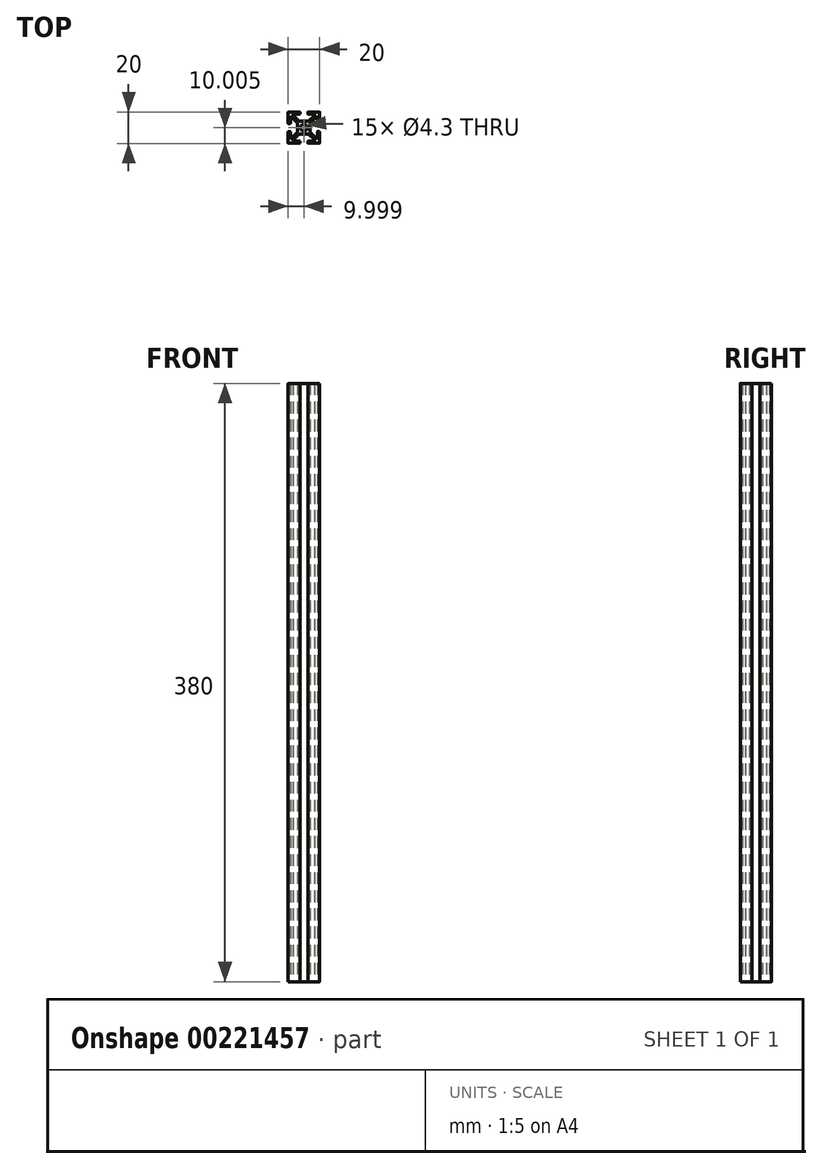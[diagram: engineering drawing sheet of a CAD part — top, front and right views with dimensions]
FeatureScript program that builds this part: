
annotation { "Feature Type Name" : "Feature", "Feature Type Description" : "" }
export const myFeature = defineFeature(function(context is Context, id is Id, definition is map)
    precondition{}
    {
        {
            var Q0;
            Q0=qCreatedBy(makeId("Top.planeOp"),FACE);
            var sketch = newSketch(context, id + "F0", { "sketchPlane" : qUnion([Q0])});
            skLineSegment(sketch, "E0.bottom", {"start": v(-9.92, 8.63) * mm, "end": v(10.08, 8.63) * mm, "construction": true});
            skLineSegment(sketch, "E0.top", {"start": v(-9.92, -11.37) * mm, "end": v(10.08, -11.37) * mm, "construction": true});
            skLineSegment(sketch, "E0.left", {"start": v(-9.92, 8.63) * mm, "end": v(-9.92, -11.37) * mm, "construction": true});
            skLineSegment(sketch, "E0.right", {"start": v(10.08, 8.63) * mm, "end": v(10.08, -11.37) * mm, "construction": true});
            skCircle(sketch, "E1", {"center": v(0.08, -1.37) * mm, "radius": 2.15 * mm});
            skPoint(sketch, "E1.centerSnap0", {"position": v(0.08, 8.63) * mm});
            skPoint(sketch, "E1.centerSnap1", {"position": v(-9.92, -1.37) * mm});
            skLineSegment(sketch, "E2.bottom", {"start": v(-3.92, 2.63) * mm, "end": v(4.08, 2.63) * mm, "construction": true});
            skLineSegment(sketch, "E2.top", {"start": v(-3.92, -5.37) * mm, "end": v(4.08, -5.37) * mm, "construction": true});
            skLineSegment(sketch, "E2.left", {"start": v(-3.92, 2.63) * mm, "end": v(-3.92, -5.37) * mm, "construction": true});
            skLineSegment(sketch, "E2.right", {"start": v(4.08, 2.63) * mm, "end": v(4.08, -5.37) * mm, "construction": true});
            skLineSegment(sketch, "E3", {"start": v(9.88, 8.63) * mm, "end": v(2.78, 8.63) * mm});
            skLineSegment(sketch, "E4.0", {"start": v(6.63, 7.13) * mm, "end": v(2.78, 7.13) * mm});
            skLineSegment(sketch, "E5", {"start": v(4.08, 2.63) * mm, "end": v(10.08, 8.63) * mm, "construction": true});
            skLineSegment(sketch, "E6.0", {"start": v(4.08, 1.57) * mm, "end": v(7.83, 5.33) * mm});
            skLineSegment(sketch, "E7.0", {"start": v(3.02, 2.63) * mm, "end": v(6.77, 6.39) * mm});
            skLineSegment(sketch, "E8", {"start": v(10.08, 8.43) * mm, "end": v(10.08, 1.33) * mm});
            skLineSegment(sketch, "E9.0", {"start": v(8.58, 5.18) * mm, "end": v(8.58, 1.33) * mm});
            skLineSegment(sketch, "E10", {"start": v(8.38, 5.38) * mm, "end": v(7.97, 5.38) * mm});
            skLineSegment(sketch, "E11", {"start": v(6.83, 6.93) * mm, "end": v(6.83, 6.53) * mm});
            skLineSegment(sketch, "E12", {"start": v(2.58, 8.43) * mm, "end": v(2.58, 7.33) * mm});
            skLineSegment(sketch, "E13", {"start": v(8.78, 1.13) * mm, "end": v(9.88, 1.13) * mm});
            skLineSegment(sketch, "E14", {"start": v(0.08, -1.37) * mm, "end": v(10.08, -1.37) * mm, "construction": true});
            skLineSegment(sketch, "E15", {"start": v(0.08, -1.37) * mm, "end": v(0.08, 8.63) * mm, "construction": true});
            skPoint(sketch, "E16.visualSharp", {"position": v(10.08, 8.63) * mm});
            skArc(sketch, "E16.filletArc", {"start": v(10.08, 8.43) * mm, "mid": v(10.02, 8.58) * mm, "end": v(9.88, 8.63) * mm});
            skPoint(sketch, "E17.visualSharp", {"position": v(2.58, 8.63) * mm});
            skArc(sketch, "E17.filletArc", {"start": v(2.78, 8.63) * mm, "mid": v(2.64, 8.58) * mm, "end": v(2.58, 8.43) * mm});
            skPoint(sketch, "E18.visualSharp", {"position": v(2.58, 7.13) * mm});
            skArc(sketch, "E18.filletArc", {"start": v(2.58, 7.33) * mm, "mid": v(2.64, 7.2) * mm, "end": v(2.78, 7.13) * mm});
            skPoint(sketch, "E19.visualSharp", {"position": v(8.58, 1.13) * mm});
            skArc(sketch, "E19.filletArc", {"start": v(8.58, 1.33) * mm, "mid": v(8.64, 1.2) * mm, "end": v(8.78, 1.13) * mm});
            skPoint(sketch, "E20.visualSharp", {"position": v(10.08, 1.13) * mm});
            skArc(sketch, "E20.filletArc", {"start": v(9.88, 1.13) * mm, "mid": v(10.02, 1.2) * mm, "end": v(10.08, 1.33) * mm});
            skPoint(sketch, "E21.visualSharp", {"position": v(6.83, 7.13) * mm});
            skArc(sketch, "E21.filletArc", {"start": v(6.83, 6.93) * mm, "mid": v(6.77, 7.08) * mm, "end": v(6.63, 7.13) * mm});
            skPoint(sketch, "E22.visualSharp", {"position": v(6.83, 6.45) * mm});
            skArc(sketch, "E22.filletArc", {"start": v(6.77, 6.39) * mm, "mid": v(6.81, 6.45) * mm, "end": v(6.83, 6.53) * mm});
            skPoint(sketch, "E23.visualSharp", {"position": v(7.89, 5.38) * mm});
            skArc(sketch, "E23.filletArc", {"start": v(7.97, 5.38) * mm, "mid": v(7.9, 5.37) * mm, "end": v(7.83, 5.33) * mm});
            skPoint(sketch, "E24.visualSharp", {"position": v(8.58, 5.38) * mm});
            skArc(sketch, "E24.filletArc", {"start": v(8.58, 5.18) * mm, "mid": v(8.52, 5.33) * mm, "end": v(8.38, 5.38) * mm});
            skLineSegment(sketch, "E25.MirrorCS", {"start": v(4.08, -4.3) * mm, "end": v(7.83, -8.06) * mm});
            skArc(sketch, "E26.MirrorCS", {"start": v(7.97, -8.12) * mm, "mid": v(7.9, -8.1) * mm, "end": v(7.83, -8.06) * mm});
            skLineSegment(sketch, "E27.MirrorCS", {"start": v(8.38, -8.12) * mm, "end": v(7.97, -8.12) * mm});
            skArc(sketch, "E28.MirrorCS", {"start": v(8.58, -7.92) * mm, "mid": v(8.52, -8.06) * mm, "end": v(8.38, -8.12) * mm});
            skLineSegment(sketch, "E29.MirrorCS", {"start": v(8.58, -7.92) * mm, "end": v(8.58, -4.07) * mm});
            skArc(sketch, "E30.MirrorCS", {"start": v(8.58, -4.07) * mm, "mid": v(8.64, -3.92) * mm, "end": v(8.78, -3.87) * mm});
            skLineSegment(sketch, "E31.MirrorCS", {"start": v(8.78, -3.87) * mm, "end": v(9.88, -3.87) * mm});
            skArc(sketch, "E32.MirrorCS", {"start": v(9.88, -3.87) * mm, "mid": v(10.02, -3.92) * mm, "end": v(10.08, -4.07) * mm});
            skLineSegment(sketch, "E33.MirrorCS", {"start": v(10.08, -11.17) * mm, "end": v(10.08, -4.07) * mm});
            skArc(sketch, "E34.MirrorCS", {"start": v(10.08, -11.17) * mm, "mid": v(10.02, -11.3) * mm, "end": v(9.88, -11.37) * mm});
            skLineSegment(sketch, "E35.MirrorCS", {"start": v(9.88, -11.37) * mm, "end": v(2.78, -11.37) * mm});
            skArc(sketch, "E36.MirrorCS", {"start": v(2.78, -11.37) * mm, "mid": v(2.64, -11.3) * mm, "end": v(2.58, -11.17) * mm});
            skLineSegment(sketch, "E37.MirrorCS", {"start": v(2.58, -11.17) * mm, "end": v(2.58, -10.07) * mm});
            skArc(sketch, "E38.MirrorCS", {"start": v(2.58, -10.07) * mm, "mid": v(2.64, -9.92) * mm, "end": v(2.78, -9.87) * mm});
            skLineSegment(sketch, "E39.MirrorCS", {"start": v(6.63, -9.87) * mm, "end": v(2.78, -9.87) * mm});
            skArc(sketch, "E40.MirrorCS", {"start": v(6.83, -9.67) * mm, "mid": v(6.77, -9.8) * mm, "end": v(6.63, -9.87) * mm});
            skLineSegment(sketch, "E41.MirrorCS", {"start": v(6.83, -9.67) * mm, "end": v(6.83, -9.26) * mm});
            skArc(sketch, "E42.MirrorCS", {"start": v(6.77, -9.12) * mm, "mid": v(6.81, -9.18) * mm, "end": v(6.83, -9.26) * mm});
            skLineSegment(sketch, "E43.MirrorCS", {"start": v(3.02, -5.37) * mm, "end": v(6.77, -9.12) * mm});
            skArc(sketch, "E44.MirrorCS", {"start": v(-9.92, 8.43) * mm, "mid": v(-9.86, 8.58) * mm, "end": v(-9.72, 8.63) * mm});
            skLineSegment(sketch, "E45.MirrorCS", {"start": v(-6.67, 6.93) * mm, "end": v(-6.67, 6.53) * mm});
            skArc(sketch, "E46.MirrorCS", {"start": v(-8.42, 5.18) * mm, "mid": v(-8.36, 5.33) * mm, "end": v(-8.22, 5.38) * mm});
            skArc(sketch, "E47.MirrorCS", {"start": v(-6.67, 6.93) * mm, "mid": v(-6.61, 7.08) * mm, "end": v(-6.47, 7.13) * mm});
            skArc(sketch, "E48.MirrorCS", {"start": v(-6.61, 6.39) * mm, "mid": v(-6.66, 6.45) * mm, "end": v(-6.67, 6.53) * mm});
            skArc(sketch, "E49.MirrorCS", {"start": v(-8.42, 1.33) * mm, "mid": v(-8.48, 1.2) * mm, "end": v(-8.62, 1.13) * mm});
            skArc(sketch, "E50.MirrorCS", {"start": v(-7.81, 5.38) * mm, "mid": v(-7.74, 5.37) * mm, "end": v(-7.67, 5.33) * mm});
            skArc(sketch, "E51.MirrorCS", {"start": v(-9.72, 1.13) * mm, "mid": v(-9.86, 1.2) * mm, "end": v(-9.92, 1.33) * mm});
            skLineSegment(sketch, "E52.MirrorCS", {"start": v(-8.22, 5.38) * mm, "end": v(-7.81, 5.38) * mm});
            skArc(sketch, "E53.MirrorCS", {"start": v(-8.42, -7.92) * mm, "mid": v(-8.36, -8.06) * mm, "end": v(-8.22, -8.12) * mm});
            skArc(sketch, "E54.MirrorCS", {"start": v(-2.42, 7.33) * mm, "mid": v(-2.48, 7.2) * mm, "end": v(-2.62, 7.13) * mm});
            skLineSegment(sketch, "E55.MirrorCS", {"start": v(-8.22, -8.12) * mm, "end": v(-7.81, -8.12) * mm});
            skArc(sketch, "E56.MirrorCS", {"start": v(-6.67, -9.67) * mm, "mid": v(-6.61, -9.8) * mm, "end": v(-6.47, -9.87) * mm});
            skLineSegment(sketch, "E57.MirrorCS", {"start": v(-6.67, -9.67) * mm, "end": v(-6.67, -9.26) * mm});
            skArc(sketch, "E58.MirrorCS", {"start": v(-9.92, -11.17) * mm, "mid": v(-9.86, -11.3) * mm, "end": v(-9.72, -11.37) * mm});
            skArc(sketch, "E59.MirrorCS", {"start": v(-9.72, -3.87) * mm, "mid": v(-9.86, -3.92) * mm, "end": v(-9.92, -4.07) * mm});
            skArc(sketch, "E60.MirrorCS", {"start": v(-6.61, -9.12) * mm, "mid": v(-6.66, -9.18) * mm, "end": v(-6.67, -9.26) * mm});
            skArc(sketch, "E61.MirrorCS", {"start": v(-2.62, -11.37) * mm, "mid": v(-2.48, -11.3) * mm, "end": v(-2.42, -11.17) * mm});
            skArc(sketch, "E62.MirrorCS", {"start": v(-8.42, -4.07) * mm, "mid": v(-8.48, -3.92) * mm, "end": v(-8.62, -3.87) * mm});
            skArc(sketch, "E63.MirrorCS", {"start": v(-7.81, -8.12) * mm, "mid": v(-7.74, -8.1) * mm, "end": v(-7.67, -8.06) * mm});
            skArc(sketch, "E64.MirrorCS", {"start": v(-2.42, -10.07) * mm, "mid": v(-2.48, -9.92) * mm, "end": v(-2.62, -9.87) * mm});
            skArc(sketch, "E65.MirrorCS", {"start": v(-2.62, 8.63) * mm, "mid": v(-2.48, 8.58) * mm, "end": v(-2.42, 8.43) * mm});
            skLineSegment(sketch, "E66.MirrorCS", {"start": v(-8.62, 1.13) * mm, "end": v(-9.72, 1.13) * mm});
            skPoint(sketch, "E67.MirrorP", {"position": v(-2.42, 7.13) * mm});
            skLineSegment(sketch, "E68.MirrorCS", {"start": v(-2.42, 8.43) * mm, "end": v(-2.42, 7.33) * mm});
            skPoint(sketch, "E69.MirrorP", {"position": v(-6.67, 7.13) * mm});
            skLineSegment(sketch, "E70.MirrorCS", {"start": v(-2.86, -5.37) * mm, "end": v(-6.61, -9.12) * mm});
            skLineSegment(sketch, "E71.MirrorCS", {"start": v(-8.62, -3.87) * mm, "end": v(-9.72, -3.87) * mm});
            skLineSegment(sketch, "E72.MirrorCS", {"start": v(-2.86, 2.63) * mm, "end": v(-6.61, 6.39) * mm});
            skLineSegment(sketch, "E73.MirrorCS", {"start": v(-8.42, -7.92) * mm, "end": v(-8.42, -4.07) * mm});
            skLineSegment(sketch, "E74.MirrorCS", {"start": v(-9.92, 8.43) * mm, "end": v(-9.92, 1.33) * mm});
            skLineSegment(sketch, "E75.MirrorCS", {"start": v(-9.72, -11.37) * mm, "end": v(-2.62, -11.37) * mm});
            skLineSegment(sketch, "E76.MirrorCS", {"start": v(-9.72, 8.63) * mm, "end": v(-2.62, 8.63) * mm});
            skLineSegment(sketch, "E77.MirrorCS", {"start": v(-2.42, -11.17) * mm, "end": v(-2.42, -10.07) * mm});
            skLineSegment(sketch, "E78.MirrorCS", {"start": v(-8.42, 5.18) * mm, "end": v(-8.42, 1.33) * mm});
            skPoint(sketch, "E79.MirrorP", {"position": v(-9.92, 8.63) * mm});
            skPoint(sketch, "E80.MirrorP", {"position": v(-8.42, 5.38) * mm});
            skLineSegment(sketch, "E81.MirrorCS", {"start": v(-6.47, 7.13) * mm, "end": v(-2.62, 7.13) * mm});
            skLineSegment(sketch, "E82.MirrorCS", {"start": v(-3.92, -4.3) * mm, "end": v(-7.67, -8.06) * mm});
            skPoint(sketch, "E83.MirrorP", {"position": v(-7.73, 5.38) * mm});
            skLineSegment(sketch, "E84.MirrorCS", {"start": v(-9.92, -11.17) * mm, "end": v(-9.92, -4.07) * mm});
            skLineSegment(sketch, "E85.MirrorCS", {"start": v(-6.47, -9.87) * mm, "end": v(-2.62, -9.87) * mm});
            skPoint(sketch, "E86.MirrorP", {"position": v(-8.42, 1.13) * mm});
            skLineSegment(sketch, "E87.MirrorCS", {"start": v(-3.92, 1.57) * mm, "end": v(-7.67, 5.33) * mm});
            skLineSegment(sketch, "E88.MirrorCS", {"start": v(-3.92, 2.63) * mm, "end": v(-9.92, 8.63) * mm, "construction": true});
            skPoint(sketch, "E89.MirrorP", {"position": v(-9.92, 1.13) * mm});
            skPoint(sketch, "E90.MirrorP", {"position": v(-6.67, 6.45) * mm});
            skPoint(sketch, "E91.MirrorP", {"position": v(-2.42, 8.63) * mm});
            skLineSegment(sketch, "E92", {"start": v(-2.86, 2.63) * mm, "end": v(3.02, 2.63) * mm});
            skLineSegment(sketch, "E93", {"start": v(4.08, 1.57) * mm, "end": v(4.08, -4.3) * mm});
            skLineSegment(sketch, "E94", {"start": v(3.02, -5.37) * mm, "end": v(-2.86, -5.37) * mm});
            skLineSegment(sketch, "E95", {"start": v(-3.92, -4.3) * mm, "end": v(-3.92, 1.57) * mm});
            skSolve(sketch);
        }
        {
            var Q0;
            Q0=makeQuery(id+"F0.imprint","IMPRINT",FACE,{"disambiguationData":[TD([[makeQuery(id+"F0.imprint","IMPRINT",EDGE,{"derivedFrom":sQuery(id+"F0.wireOp",EDGE,"E1")}),-1.0]])]});
            extrude(context, id + "F1", {"entities" : qUnion([Q0]), "depth" : 380 * mm});
        }
    });
